# Revit family: assa_abloy_versamax_31
name_source: partatom
category: Doors
units: mm (PartAtom-declared; Revit-internal decimal feet)

## family parameters
Always vertical = Yes
Classification Number = 23.30.10.00
Cut with Voids When Loaded = No
Host = Wall
Room Calculation Point = No
Shared = No

## types (3) — shared parameters
Analytic Construction = <None>
BIMobject category = Swing Doors
Bottom Profile Height = Swing Versamax Leaf : 0' 4''
Bottom Profile Option 01 = Swing Versamax Leaf : 0' 4''
Bottom Profile Option 02 = Swing Versamax Leaf : 0' 7''
Bottom Profile Option 03 = Swing Versamax Leaf : 0' 10''
Brass Polished Finish = Brass, Polished
Brass Satin Finish = Brass, Satin
Clear Anodized = Clear Anodized
Dark Bronze Anodized = Dark Bronze Anodized
Date of publishing = 2015-02-23
Depth = 0.00
Edition number = 1
Frame Material = Clear Anodized
Gap = 0' - 0 1/4"
Glass = Glass
Height = 7' - 5 3/4"
IFC Classification = Door
Manufacturer = ASSA ABLOY Entrance Systems-North America
Manufacturer name = ASSA ABLOY Entrance Systems-North America
Material main = Aluminium
Nominal height = 0.00
Nominal width = 0.00
Product SKU = VersaMax_Swing_OHC
Product data url = http://besam-na.bimobject.com
Product family = ICU
Product group = Swing
QR code = http://besam-na.bimobject.com
Rough Height = 7' - 6"
Rubber = Rubber, Black
Stainless Steel Polished Finish = Stainless Steel, Polished
Stainless Steel Satin Finish = Stainless Steel, Satin
Thickness = 0' - 0"
UNSPSC Code = 30171511
Uniclass 1.4 Code = L81323
Uniclass 1.4 Description = Swings
Wall Closure = By host
Weight Net (Kg) = 0

## per-type parameters (varying)
| type | Rough Width | Width |
| 75 1/2" | 6' - 4" | 6' - 3 1/2" |
| 87 1/2" | 7' - 4" | 7' - 3 1/2" |
| 99 1/2" | 8' - 4" | 8' - 3 1/2" |

## geometry (parser evidence)
native form markers: Sweep x26
no freeform markers — native parametric forms only
